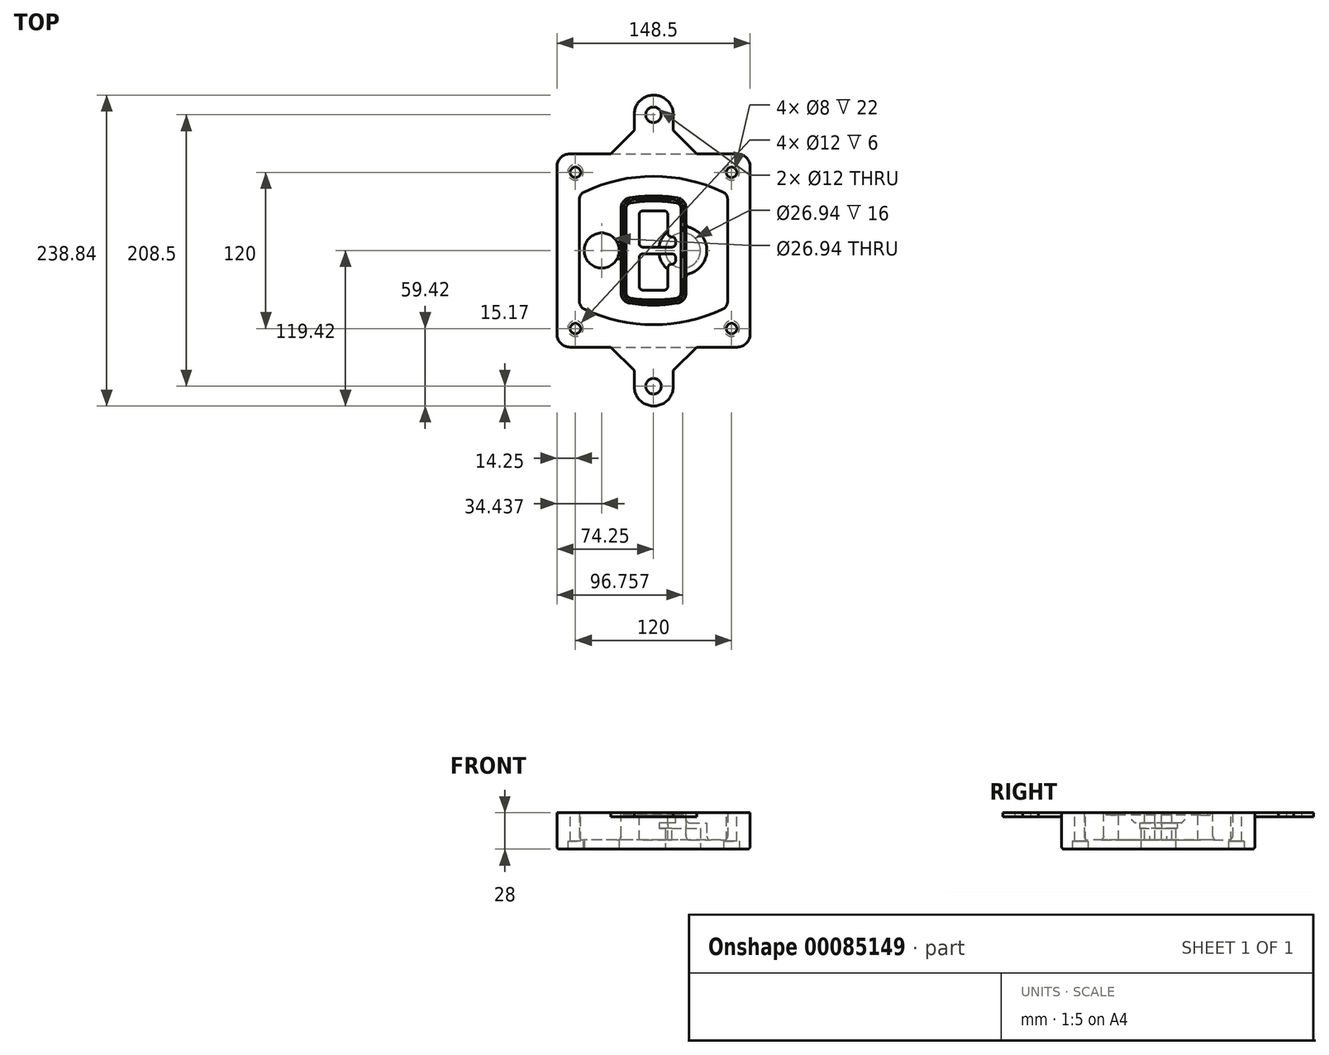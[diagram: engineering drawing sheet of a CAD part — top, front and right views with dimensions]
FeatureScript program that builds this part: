
annotation { "Feature Type Name" : "Feature", "Feature Type Description" : "" }
export const myFeature = defineFeature(function(context is Context, id is Id, definition is map)
    precondition{}
    {
        {
            var Q0;
            Q0=qCreatedBy(makeId("Top.planeOp"),FACE);
            var sketch = newSketch(context, id + "F0", { "sketchPlane" : qUnion([Q0])});
            skPoint(sketch, "E0.rect.middle", {"position": v(0, 0) * mm});
            skLineSegment(sketch, "E1.bottom", {"start": v(-64.25, -74.25) * mm, "end": v(64.25, -74.25) * mm});
            skLineSegment(sketch, "E1.top", {"start": v(-64.25, 74.25) * mm, "end": v(64.25, 74.25) * mm});
            skLineSegment(sketch, "E1.left", {"start": v(-74.25, -64.25) * mm, "end": v(-74.25, 64.25) * mm});
            skLineSegment(sketch, "E1.right", {"start": v(74.25, -64.25) * mm, "end": v(74.25, 64.25) * mm});
            skLineSegment(sketch, "E2", {"start": v(-74.25, 74.25) * mm, "end": v(74.25, -74.25) * mm, "construction": true});
            skLineSegment(sketch, "E3", {"start": v(74.25, 74.25) * mm, "end": v(-74.25, -74.25) * mm, "construction": true});
            skCircle(sketch, "E4", {"center": v(-60, 60) * mm, "radius": 4 * mm});
            skCircle(sketch, "E5", {"center": v(60, 60) * mm, "radius": 4 * mm});
            skCircle(sketch, "E6", {"center": v(60, -60) * mm, "radius": 4 * mm});
            skCircle(sketch, "E7", {"center": v(-60, -60) * mm, "radius": 4 * mm});
            skLineSegment(sketch, "E8", {"start": v(-60, 60) * mm, "end": v(60, 60) * mm, "construction": true});
            skLineSegment(sketch, "E9", {"start": v(60, 60) * mm, "end": v(60, -60) * mm, "construction": true});
            skLineSegment(sketch, "E10", {"start": v(60, -60) * mm, "end": v(-60, -60) * mm, "construction": true});
            skLineSegment(sketch, "E11", {"start": v(-60, -60) * mm, "end": v(-60, 60) * mm, "construction": true});
            skLineSegment(sketch, "E12", {"start": v(-60, 38.83) * mm, "end": v(-60, -38.83) * mm});
            skLineSegment(sketch, "E13", {"start": v(60, 38.83) * mm, "end": v(60, -38.83) * mm});
            skArc(sketch, "E14", {"start": v(54.26, 47.88) * mm, "mid": v(0, 60) * mm, "end": v(-54.26, 47.88) * mm});
            skArc(sketch, "E15", {"start": v(-54.26, -47.88) * mm, "mid": v(0, -60) * mm, "end": v(54.26, -47.88) * mm});
            skLineSegment(sketch, "E16", {"start": v(-60, 0) * mm, "end": v(60, 0) * mm, "construction": true});
            skPoint(sketch, "E17.visualSharp", {"position": v(-60, -45) * mm});
            skArc(sketch, "E17.filletArc", {"start": v(-60, -38.83) * mm, "mid": v(-58.44, -44.2) * mm, "end": v(-54.26, -47.88) * mm});
            skPoint(sketch, "E18.visualSharp", {"position": v(-60, 45) * mm});
            skArc(sketch, "E18.filletArc", {"start": v(-54.26, 47.88) * mm, "mid": v(-58.44, 44.2) * mm, "end": v(-60, 38.83) * mm});
            skPoint(sketch, "E19.visualSharp", {"position": v(60, 45) * mm});
            skArc(sketch, "E19.filletArc", {"start": v(60, 38.83) * mm, "mid": v(58.44, 44.2) * mm, "end": v(54.26, 47.88) * mm});
            skPoint(sketch, "E20.visualSharp", {"position": v(60, -45) * mm});
            skArc(sketch, "E20.filletArc", {"start": v(54.26, -47.88) * mm, "mid": v(58.44, -44.2) * mm, "end": v(60, -38.83) * mm});
            skPoint(sketch, "E21.visualSharp", {"position": v(-74.25, 74.25) * mm});
            skArc(sketch, "E21.filletArc", {"start": v(-64.25, 74.25) * mm, "mid": v(-71.32, 71.32) * mm, "end": v(-74.25, 64.25) * mm});
            skPoint(sketch, "E22.visualSharp", {"position": v(74.25, 74.25) * mm});
            skArc(sketch, "E22.filletArc", {"start": v(74.25, 64.25) * mm, "mid": v(71.32, 71.32) * mm, "end": v(64.25, 74.25) * mm});
            skPoint(sketch, "E23.visualSharp", {"position": v(74.25, -74.25) * mm});
            skArc(sketch, "E23.filletArc", {"start": v(64.25, -74.25) * mm, "mid": v(71.32, -71.32) * mm, "end": v(74.25, -64.25) * mm});
            skPoint(sketch, "E24.visualSharp", {"position": v(-74.25, -74.25) * mm});
            skArc(sketch, "E24.filletArc", {"start": v(-74.25, -64.25) * mm, "mid": v(-71.32, -71.32) * mm, "end": v(-64.25, -74.25) * mm});
            skArc(sketch, "E25.0", {"start": v(57, 38.83) * mm, "mid": v(55.9, 42.58) * mm, "end": v(52.98, 45.17) * mm});
            skLineSegment(sketch, "E25.1", {"start": v(57, 38.83) * mm, "end": v(57, -38.83) * mm});
            skArc(sketch, "E25.2", {"start": v(52.98, -45.17) * mm, "mid": v(55.9, -42.58) * mm, "end": v(57, -38.83) * mm});
            skArc(sketch, "E25.3", {"start": v(-52.98, -45.17) * mm, "mid": v(0, -57) * mm, "end": v(52.98, -45.17) * mm});
            skArc(sketch, "E25.4", {"start": v(-57, -38.83) * mm, "mid": v(-55.9, -42.58) * mm, "end": v(-52.98, -45.17) * mm});
            skArc(sketch, "E25.5", {"start": v(52.98, 45.17) * mm, "mid": v(0, 57) * mm, "end": v(-52.98, 45.17) * mm});
            skLineSegment(sketch, "E25.6", {"start": v(-57, 38.83) * mm, "end": v(-57, -38.83) * mm});
            skArc(sketch, "E25.7", {"start": v(-52.98, 45.17) * mm, "mid": v(-55.9, 42.58) * mm, "end": v(-57, 38.83) * mm});
            skArc(sketch, "E26.0", {"start": v(-55.96, 51.5) * mm, "mid": v(-61.82, 46.33) * mm, "end": v(-64, 38.83) * mm});
            skArc(sketch, "E26.1", {"start": v(55.96, 51.5) * mm, "mid": v(0, 64) * mm, "end": v(-55.96, 51.5) * mm});
            skArc(sketch, "E26.2", {"start": v(64, 38.83) * mm, "mid": v(61.82, 46.33) * mm, "end": v(55.96, 51.5) * mm});
            skLineSegment(sketch, "E26.3", {"start": v(64, 38.83) * mm, "end": v(64, -38.83) * mm});
            skArc(sketch, "E26.4", {"start": v(55.96, -51.5) * mm, "mid": v(61.82, -46.33) * mm, "end": v(64, -38.83) * mm});
            skLineSegment(sketch, "E26.5", {"start": v(-64, 38.83) * mm, "end": v(-64, -38.83) * mm});
            skArc(sketch, "E26.6", {"start": v(-55.96, -51.5) * mm, "mid": v(0, -64) * mm, "end": v(55.96, -51.5) * mm});
            skArc(sketch, "E26.7", {"start": v(-64, -38.83) * mm, "mid": v(-61.82, -46.33) * mm, "end": v(-55.96, -51.5) * mm});
            skSolve(sketch);
        }
        {
            var Q0;
            Q0=makeQuery(id+"F0.imprint","IMPRINT",FACE,{"disambiguationData":[TD([[makeQuery(id+"F0.imprint","IMPRINT",EDGE,{"derivedFrom":sQuery(id+"F0.wireOp",EDGE,"E1.bottom")}),1.0]])]});
            var Q1;
            Q1=makeQuery(id+"F0.imprint","IMPRINT",FACE,{"disambiguationData":[TD([[makeQuery(id+"F0.imprint","IMPRINT",EDGE,{"derivedFrom":sQuery(id+"F0.wireOp",EDGE,"E12")}),1.0]])]});
            var Q2;
            Q2=makeQuery(id+"F0.imprint","IMPRINT",FACE,{"disambiguationData":[TD([[makeQuery(id+"F0.imprint","IMPRINT",EDGE,{"derivedFrom":sQuery(id+"F0.wireOp",EDGE,"E25.0")}),1.0]])]});
            var Q3;
            Q3=makeQuery(id+"F0.imprint","IMPRINT",FACE,{"disambiguationData":[TD([[makeQuery(id+"F0.imprint","IMPRINT",EDGE,{"derivedFrom":sQuery(id+"F0.wireOp",EDGE,"E12")}),-1.0]])]});
            extrude(context, id + "F1", {"entities" : qUnion([Q0, Q1, Q2, Q3]), "oppositeDirection" : true, "depth" : 25 * mm});
        }
        {
            var Q0;
            Q0=makeQuery(id+"F0.imprint","IMPRINT",FACE,{"disambiguationData":[TD([[makeQuery(id+"F0.imprint","IMPRINT",EDGE,{"derivedFrom":sQuery(id+"F0.wireOp",EDGE,"E12")}),1.0]])]});
            extrude(context, id + "F2", {"entities" : qUnion([Q0]), "operationType" : NewBodyOperationType.ADD, "depth" : 3 * mm});
        }
        {
            var Q0;
            Q0=makeQuery(id+"F0.imprint","IMPRINT",FACE,{"disambiguationData":[TD([[makeQuery(id+"F0.imprint","IMPRINT",EDGE,{"derivedFrom":sQuery(id+"F0.wireOp",EDGE,"E25.0")}),1.0]])]});
            extrude(context, id + "F3", {"entities" : qUnion([Q0]), "operationType" : NewBodyOperationType.REMOVE, "oppositeDirection" : true, "depth" : 18 * mm});
        }
        {
            var Q0;
            Q0=makeQuery(id+"F2.opExtrude","CAP_FACE",FACE,{"disambiguationData":[OSD([sQuery(id+"F0.wireOp",EDGE,"E12"),sQuery(id+"F0.wireOp",EDGE,"E13"),sQuery(id+"F0.wireOp",EDGE,"E14"),sQuery(id+"F0.wireOp",EDGE,"E15"),sQuery(id+"F0.wireOp",EDGE,"E17.filletArc"),sQuery(id+"F0.wireOp",EDGE,"E18.filletArc"),sQuery(id+"F0.wireOp",EDGE,"E19.filletArc"),sQuery(id+"F0.wireOp",EDGE,"E20.filletArc"),sQuery(id+"F0.wireOp",EDGE,"E25.0"),sQuery(id+"F0.wireOp",EDGE,"E25.1"),sQuery(id+"F0.wireOp",EDGE,"E25.2"),sQuery(id+"F0.wireOp",EDGE,"E25.3"),sQuery(id+"F0.wireOp",EDGE,"E25.4"),sQuery(id+"F0.wireOp",EDGE,"E25.5"),sQuery(id+"F0.wireOp",EDGE,"E25.6"),sQuery(id+"F0.wireOp",EDGE,"E25.7")])],"isStart":false});
            var sketch = newSketch(context, id + "F4", { "sketchPlane" : qUnion([Q0])});
            skArc(sketch, "E27.0", {"start": v(-18.34, -40.45) * mm, "mid": v(0, -42) * mm, "end": v(18.34, -40.45) * mm});
            skArc(sketch, "E28.0", {"start": v(18.34, 40.45) * mm, "mid": v(0, 42) * mm, "end": v(-18.34, 40.45) * mm});
            skLineSegment(sketch, "E29", {"start": v(-25, 32.57) * mm, "end": v(-25, -32.57) * mm});
            skLineSegment(sketch, "E30", {"start": v(25, 32.57) * mm, "end": v(25, -32.57) * mm});
            skLineSegment(sketch, "E31", {"start": v(-25, 39.1) * mm, "end": v(25, 39.1) * mm, "construction": true});
            skLineSegment(sketch, "E32", {"start": v(-25, -39.1) * mm, "end": v(25, -39.1) * mm, "construction": true});
            skPoint(sketch, "E33.visualSharp", {"position": v(-25, 39.1) * mm});
            skArc(sketch, "E33.filletArc", {"start": v(-18.34, 40.45) * mm, "mid": v(-23.11, 37.73) * mm, "end": v(-25, 32.57) * mm});
            skPoint(sketch, "E34.visualSharp", {"position": v(25, 39.1) * mm});
            skArc(sketch, "E34.filletArc", {"start": v(25, 32.57) * mm, "mid": v(23.11, 37.73) * mm, "end": v(18.34, 40.45) * mm});
            skPoint(sketch, "E35.visualSharp", {"position": v(25, -39.1) * mm});
            skArc(sketch, "E35.filletArc", {"start": v(18.34, -40.45) * mm, "mid": v(23.11, -37.73) * mm, "end": v(25, -32.57) * mm});
            skPoint(sketch, "E36.visualSharp", {"position": v(-25, -39.1) * mm});
            skArc(sketch, "E36.filletArc", {"start": v(-25, -32.57) * mm, "mid": v(-23.11, -37.73) * mm, "end": v(-18.34, -40.45) * mm});
            skArc(sketch, "E37.0", {"start": v(52.98, 45.17) * mm, "mid": v(0, 57) * mm, "end": v(-52.98, 45.17) * mm});
            skArc(sketch, "E37.1", {"start": v(-52.98, 45.17) * mm, "mid": v(-55.9, 42.58) * mm, "end": v(-57, 38.83) * mm});
            skLineSegment(sketch, "E37.2", {"start": v(-57, 38.83) * mm, "end": v(-57, -38.83) * mm});
            skArc(sketch, "E37.3", {"start": v(-57, -38.83) * mm, "mid": v(-55.9, -42.58) * mm, "end": v(-52.98, -45.17) * mm});
            skArc(sketch, "E37.4", {"start": v(-52.98, -45.17) * mm, "mid": v(0, -57) * mm, "end": v(52.98, -45.17) * mm});
            skArc(sketch, "E37.5", {"start": v(52.98, -45.17) * mm, "mid": v(55.9, -42.58) * mm, "end": v(57, -38.83) * mm});
            skLineSegment(sketch, "E37.6", {"start": v(57, 38.83) * mm, "end": v(57, -38.83) * mm});
            skArc(sketch, "E37.7", {"start": v(57, 38.83) * mm, "mid": v(55.9, 42.58) * mm, "end": v(52.98, 45.17) * mm});
            skLineSegment(sketch, "E38.0", {"start": v(23, 32.57) * mm, "end": v(23, -32.57) * mm});
            skArc(sketch, "E38.1", {"start": v(18, -38.48) * mm, "mid": v(21.58, -36.44) * mm, "end": v(23, -32.57) * mm});
            skArc(sketch, "E38.2", {"start": v(-18, -38.48) * mm, "mid": v(0, -40) * mm, "end": v(18, -38.48) * mm});
            skArc(sketch, "E38.3", {"start": v(-23, -32.57) * mm, "mid": v(-21.58, -36.44) * mm, "end": v(-18, -38.48) * mm});
            skLineSegment(sketch, "E38.4", {"start": v(-23, 32.57) * mm, "end": v(-23, -32.57) * mm});
            skArc(sketch, "E38.5", {"start": v(23, 32.57) * mm, "mid": v(21.58, 36.44) * mm, "end": v(18, 38.48) * mm});
            skArc(sketch, "E38.6", {"start": v(-18, 38.48) * mm, "mid": v(-21.58, 36.44) * mm, "end": v(-23, 32.57) * mm});
            skArc(sketch, "E38.7", {"start": v(18, 38.48) * mm, "mid": v(0, 40) * mm, "end": v(-18, 38.48) * mm});
            skArc(sketch, "E39.0", {"start": v(21, 32.57) * mm, "mid": v(20.06, 35.15) * mm, "end": v(17.67, 36.5) * mm});
            skLineSegment(sketch, "E39.1", {"start": v(21, 32.57) * mm, "end": v(21, -32.57) * mm});
            skArc(sketch, "E39.2", {"start": v(17.67, -36.5) * mm, "mid": v(20.06, -35.15) * mm, "end": v(21, -32.57) * mm});
            skArc(sketch, "E39.3", {"start": v(-17.67, -36.5) * mm, "mid": v(0, -38) * mm, "end": v(17.67, -36.5) * mm});
            skArc(sketch, "E39.4", {"start": v(-21, -32.57) * mm, "mid": v(-20.06, -35.15) * mm, "end": v(-17.67, -36.5) * mm});
            skArc(sketch, "E39.5", {"start": v(17.67, 36.5) * mm, "mid": v(0, 38) * mm, "end": v(-17.67, 36.5) * mm});
            skLineSegment(sketch, "E39.6", {"start": v(-21, 32.57) * mm, "end": v(-21, -32.57) * mm});
            skArc(sketch, "E39.7", {"start": v(-17.67, 36.5) * mm, "mid": v(-20.06, 35.15) * mm, "end": v(-21, 32.57) * mm});
            skLineSegment(sketch, "E40", {"start": v(-25, 0) * mm, "end": v(25, 0) * mm, "construction": true});
            skLineSegment(sketch, "E41", {"start": v(-11, 5.5) * mm, "end": v(-11, 27.5) * mm});
            skLineSegment(sketch, "E42", {"start": v(-8, 30.5) * mm, "end": v(8, 30.5) * mm});
            skLineSegment(sketch, "E43", {"start": v(11, 27.5) * mm, "end": v(11, 13.5) * mm});
            skLineSegment(sketch, "E44", {"start": v(14, 10.5) * mm, "end": v(14, 10.5) * mm});
            skLineSegment(sketch, "E45", {"start": v(17, 7.5) * mm, "end": v(17, 5.5) * mm});
            skLineSegment(sketch, "E46", {"start": v(14, 2.5) * mm, "end": v(-8, 2.5) * mm});
            skPoint(sketch, "E47.visualSharp", {"position": v(-11, 30.5) * mm});
            skArc(sketch, "E47.filletArc", {"start": v(-8, 30.5) * mm, "mid": v(-10.12, 29.62) * mm, "end": v(-11, 27.5) * mm});
            skPoint(sketch, "E48.visualSharp", {"position": v(11, 30.5) * mm});
            skArc(sketch, "E48.filletArc", {"start": v(11, 27.5) * mm, "mid": v(10.12, 29.62) * mm, "end": v(8, 30.5) * mm});
            skPoint(sketch, "E49.visualSharp", {"position": v(11, 10.5) * mm});
            skArc(sketch, "E49.filletArc", {"start": v(11, 13.5) * mm, "mid": v(11.88, 11.38) * mm, "end": v(14, 10.5) * mm});
            skPoint(sketch, "E50.visualSharp", {"position": v(17, 10.5) * mm});
            skArc(sketch, "E50.filletArc", {"start": v(17, 7.5) * mm, "mid": v(16.12, 9.62) * mm, "end": v(14, 10.5) * mm});
            skPoint(sketch, "E51.visualSharp", {"position": v(17, 2.5) * mm});
            skArc(sketch, "E51.filletArc", {"start": v(14, 2.5) * mm, "mid": v(16.12, 3.38) * mm, "end": v(17, 5.5) * mm});
            skPoint(sketch, "E52.visualSharp", {"position": v(-11, 2.5) * mm});
            skArc(sketch, "E52.filletArc", {"start": v(-11, 5.5) * mm, "mid": v(-10.12, 3.38) * mm, "end": v(-8, 2.5) * mm});
            skLineSegment(sketch, "E53.0.MirrorCS", {"start": v(14, -2.5) * mm, "end": v(-8, -2.5) * mm});
            skArc(sketch, "E54.0.MirrorCS", {"start": v(-11, -5.5) * mm, "mid": v(-10.12, -3.38) * mm, "end": v(-8, -2.5) * mm});
            skLineSegment(sketch, "E55.0.MirrorCS", {"start": v(-11, -5.5) * mm, "end": v(-11, -27.5) * mm});
            skArc(sketch, "E56.0.MirrorCS", {"start": v(-8, -30.5) * mm, "mid": v(-10.12, -29.62) * mm, "end": v(-11, -27.5) * mm});
            skLineSegment(sketch, "E57.0.MirrorCS", {"start": v(-8, -30.5) * mm, "end": v(8, -30.5) * mm});
            skArc(sketch, "E58.0.MirrorCS", {"start": v(11, -27.5) * mm, "mid": v(10.12, -29.62) * mm, "end": v(8, -30.5) * mm});
            skLineSegment(sketch, "E59.0.MirrorCS", {"start": v(11, -27.5) * mm, "end": v(11, -13.5) * mm});
            skArc(sketch, "E60.0.MirrorCS", {"start": v(11, -13.5) * mm, "mid": v(11.88, -11.38) * mm, "end": v(14, -10.5) * mm});
            skArc(sketch, "E61.0.MirrorCS", {"start": v(17, -7.5) * mm, "mid": v(16.12, -9.62) * mm, "end": v(14, -10.5) * mm});
            skLineSegment(sketch, "E62.0.MirrorCS", {"start": v(17, -7.5) * mm, "end": v(17, -5.5) * mm});
            skArc(sketch, "E63.0.MirrorCS", {"start": v(14, -2.5) * mm, "mid": v(16.12, -3.38) * mm, "end": v(17, -5.5) * mm});
            skSolve(sketch);
        }
        {
            var Q0;
            Q0=makeQuery(id+"F4.imprint","IMPRINT",FACE,{"disambiguationData":[TD([[makeQuery(id+"F4.imprint","IMPRINT",EDGE,{"derivedFrom":sQuery(id+"F4.wireOp",EDGE,"E27.0")}),1.0]])]});
            var Q1;
            Q1=makeQuery(id+"F4.imprint","IMPRINT",FACE,{"disambiguationData":[TD([[makeQuery(id+"F4.imprint","IMPRINT",EDGE,{"derivedFrom":sQuery(id+"F4.wireOp",EDGE,"E38.0")}),-1.0]])]});
            var Q2;
            Q2=makeQuery(id+"F4.imprint","IMPRINT",FACE,{"disambiguationData":[TD([[makeQuery(id+"F4.imprint","IMPRINT",EDGE,{"derivedFrom":sQuery(id+"F4.wireOp",EDGE,"E39.0")}),1.0]])]});
            extrude(context, id + "F5", {"entities" : qUnion([Q0, Q1, Q2]), "operationType" : NewBodyOperationType.ADD, "endBound" : BoundingType.UP_TO_NEXT, "oppositeDirection" : true, "depth" : 25 * mm});
        }
        {
            var Q0;
            Q0=makeQuery(id+"F4.imprint","IMPRINT",FACE,{"disambiguationData":[TD([[makeQuery(id+"F4.imprint","IMPRINT",EDGE,{"derivedFrom":sQuery(id+"F4.wireOp",EDGE,"E38.0")}),-1.0]])]});
            extrude(context, id + "F6", {"entities" : qUnion([Q0]), "operationType" : NewBodyOperationType.REMOVE, "oppositeDirection" : true, "depth" : 2 * mm});
        }
        {
            var Q0;
            Q0=makeQuery(id+"F1.opExtrude","CAP_FACE",FACE,{"disambiguationData":[OSD([sQuery(id+"F0.wireOp",EDGE,"E1.bottom"),sQuery(id+"F0.wireOp",EDGE,"E1.top"),sQuery(id+"F0.wireOp",EDGE,"E1.left"),sQuery(id+"F0.wireOp",EDGE,"E1.right"),sQuery(id+"F0.wireOp",EDGE,"E4"),sQuery(id+"F0.wireOp",EDGE,"E5"),sQuery(id+"F0.wireOp",EDGE,"E6"),sQuery(id+"F0.wireOp",EDGE,"E7"),sQuery(id+"F0.wireOp",EDGE,"E21.filletArc"),sQuery(id+"F0.wireOp",EDGE,"E22.filletArc"),sQuery(id+"F0.wireOp",EDGE,"E23.filletArc"),sQuery(id+"F0.wireOp",EDGE,"E24.filletArc")])],"isStart":false});
            var sketch = newSketch(context, id + "F7", { "sketchPlane" : qUnion([Q0])});
            skCircle(sketch, "E64", {"center": v(22.5, 0) * mm, "radius": 13.47 * mm});
            skCircle(sketch, "E65", {"center": v(-39.81, 0) * mm, "radius": 13.47 * mm});
            skLineSegment(sketch, "E66", {"start": v(74.25, 0) * mm, "end": v(-74.25, 0) * mm});
            skCircle(sketch, "E67", {"center": v(22.5, 0) * mm, "radius": 18.47 * mm});
            skCircle(sketch, "E68", {"center": v(60, -60) * mm, "radius": 6 * mm});
            skCircle(sketch, "E69", {"center": v(-60, -60) * mm, "radius": 6 * mm});
            skCircle(sketch, "E70", {"center": v(-60, 60) * mm, "radius": 6 * mm});
            skCircle(sketch, "E71", {"center": v(60, 60) * mm, "radius": 6 * mm});
            skSolve(sketch);
        }
        {
            var Q0;
            {var subQ1=sQuery(id+"F7.wireOp",EDGE,"E66");var subQ4=sQuery(id+"F7.wireOp",EDGE,"E64");var subQ6=makeQuery(id+"F7.imprint","INTERSECT",VERTEX,{"disambiguationData":[OD(0.0)],"derivedFrom":[subQ4,subQ1]});Q0=makeQuery(id+"F7.imprint","IMPRINT",FACE,{"disambiguationData":[TD([[makeQuery(id+"F7.imprint","IMPRINT",EDGE,{"disambiguationData":[TD([[subQ6,-1.0]])],"derivedFrom":subQ4}),-1.0]])]});}
            var Q1;
            {var subQ0=sQuery(id+"F7.wireOp",EDGE,"E66");var subQ1=sQuery(id+"F7.wireOp",EDGE,"E64");var subQ3=makeQuery(id+"F7.imprint","INTERSECT",VERTEX,{"disambiguationData":[OD(0.0)],"derivedFrom":[subQ1,subQ0]});Q1=makeQuery(id+"F7.imprint","IMPRINT",FACE,{"disambiguationData":[TD([[makeQuery(id+"F7.imprint","IMPRINT",EDGE,{"disambiguationData":[TD([[subQ3,-1.0]])],"derivedFrom":subQ1}),1.0]])]});}
            var Q2;
            {var subQ0=sQuery(id+"F7.wireOp",EDGE,"E66");var subQ1=sQuery(id+"F7.wireOp",EDGE,"E64");var subQ3=makeQuery(id+"F7.imprint","INTERSECT",VERTEX,{"disambiguationData":[OD(0.0)],"derivedFrom":[subQ1,subQ0]});Q2=makeQuery(id+"F7.imprint","IMPRINT",FACE,{"disambiguationData":[TD([[makeQuery(id+"F7.imprint","IMPRINT",EDGE,{"disambiguationData":[TD([[subQ3,1.0]])],"derivedFrom":subQ1}),1.0]])]});}
            var Q3;
            {var subQ1=sQuery(id+"F7.wireOp",EDGE,"E66");var subQ4=sQuery(id+"F7.wireOp",EDGE,"E64");var subQ6=makeQuery(id+"F7.imprint","INTERSECT",VERTEX,{"disambiguationData":[OD(0.0)],"derivedFrom":[subQ4,subQ1]});Q3=makeQuery(id+"F7.imprint","IMPRINT",FACE,{"disambiguationData":[TD([[makeQuery(id+"F7.imprint","IMPRINT",EDGE,{"disambiguationData":[TD([[subQ6,1.0]])],"derivedFrom":subQ4}),-1.0]])]});}
            extrude(context, id + "F8", {"entities" : qUnion([Q0, Q1, Q2, Q3]), "operationType" : NewBodyOperationType.ADD, "oppositeDirection" : true, "depth" : 20 * mm});
        }
        {
            var Q0;
            {var subQ0=sQuery(id+"F7.wireOp",EDGE,"E66");var subQ1=sQuery(id+"F7.wireOp",EDGE,"E64");var subQ3=makeQuery(id+"F7.imprint","INTERSECT",VERTEX,{"disambiguationData":[OD(0.0)],"derivedFrom":[subQ1,subQ0]});Q0=makeQuery(id+"F7.imprint","IMPRINT",FACE,{"disambiguationData":[TD([[makeQuery(id+"F7.imprint","IMPRINT",EDGE,{"disambiguationData":[TD([[subQ3,-1.0]])],"derivedFrom":subQ1}),1.0]])]});}
            var Q1;
            {var subQ0=sQuery(id+"F7.wireOp",EDGE,"E66");var subQ1=sQuery(id+"F7.wireOp",EDGE,"E64");var subQ3=makeQuery(id+"F7.imprint","INTERSECT",VERTEX,{"disambiguationData":[OD(0.0)],"derivedFrom":[subQ1,subQ0]});Q1=makeQuery(id+"F7.imprint","IMPRINT",FACE,{"disambiguationData":[TD([[makeQuery(id+"F7.imprint","IMPRINT",EDGE,{"disambiguationData":[TD([[subQ3,1.0]])],"derivedFrom":subQ1}),1.0]])]});}
            extrude(context, id + "F9", {"entities" : qUnion([Q0, Q1]), "operationType" : NewBodyOperationType.REMOVE, "oppositeDirection" : true, "depth" : 16 * mm});
        }
        {
            var Q0;
            {var subQ0=sQuery(id+"F7.wireOp",EDGE,"E66");var subQ1=sQuery(id+"F7.wireOp",EDGE,"E65");var subQ3=makeQuery(id+"F7.imprint","INTERSECT",VERTEX,{"disambiguationData":[OD(0.0)],"derivedFrom":[subQ1,subQ0]});Q0=makeQuery(id+"F7.imprint","IMPRINT",FACE,{"disambiguationData":[TD([[makeQuery(id+"F7.imprint","IMPRINT",EDGE,{"disambiguationData":[TD([[subQ3,-1.0]])],"derivedFrom":subQ1}),1.0]])]});}
            var Q1;
            {var subQ0=sQuery(id+"F7.wireOp",EDGE,"E66");var subQ1=sQuery(id+"F7.wireOp",EDGE,"E65");var subQ3=makeQuery(id+"F7.imprint","INTERSECT",VERTEX,{"disambiguationData":[OD(0.0)],"derivedFrom":[subQ1,subQ0]});Q1=makeQuery(id+"F7.imprint","IMPRINT",FACE,{"disambiguationData":[TD([[makeQuery(id+"F7.imprint","IMPRINT",EDGE,{"disambiguationData":[TD([[subQ3,1.0]])],"derivedFrom":subQ1}),1.0]])]});}
            extrude(context, id + "F10", {"entities" : qUnion([Q0, Q1]), "operationType" : NewBodyOperationType.REMOVE, "oppositeDirection" : true, "depth" : 25 * mm});
        }
        {
            var Q0;
            Q0=makeQuery(id+"F7.imprint","IMPRINT",FACE,{"disambiguationData":[TD([[makeQuery(id+"F7.imprint","IMPRINT",EDGE,{"derivedFrom":sQuery(id+"F7.wireOp",EDGE,"E68")}),1.0]])]});
            var Q1;
            Q1=makeQuery(id+"F7.imprint","IMPRINT",FACE,{"disambiguationData":[TD([[makeQuery(id+"F7.imprint","IMPRINT",EDGE,{"derivedFrom":makeQuery(id+"F1.opExtrude","CAP_EDGE",EDGE,{"disambiguationData":[OSD([sQuery(id+"F0.wireOp",EDGE,"E5")])],"isStart":false})}),-1.0]])]});
            var Q2;
            Q2=makeQuery(id+"F7.imprint","IMPRINT",FACE,{"disambiguationData":[TD([[makeQuery(id+"F7.imprint","IMPRINT",EDGE,{"derivedFrom":sQuery(id+"F7.wireOp",EDGE,"E69")}),1.0]])]});
            var Q3;
            Q3=makeQuery(id+"F7.imprint","IMPRINT",FACE,{"disambiguationData":[TD([[makeQuery(id+"F7.imprint","IMPRINT",EDGE,{"derivedFrom":makeQuery(id+"F1.opExtrude","CAP_EDGE",EDGE,{"disambiguationData":[OSD([sQuery(id+"F0.wireOp",EDGE,"E4")])],"isStart":false})}),-1.0]])]});
            var Q4;
            Q4=makeQuery(id+"F7.imprint","IMPRINT",FACE,{"disambiguationData":[TD([[makeQuery(id+"F7.imprint","IMPRINT",EDGE,{"derivedFrom":sQuery(id+"F7.wireOp",EDGE,"E70")}),1.0]])]});
            var Q5;
            Q5=makeQuery(id+"F7.imprint","IMPRINT",FACE,{"disambiguationData":[TD([[makeQuery(id+"F7.imprint","IMPRINT",EDGE,{"derivedFrom":makeQuery(id+"F1.opExtrude","CAP_EDGE",EDGE,{"disambiguationData":[OSD([sQuery(id+"F0.wireOp",EDGE,"E7")])],"isStart":false})}),-1.0]])]});
            var Q6;
            Q6=makeQuery(id+"F7.imprint","IMPRINT",FACE,{"disambiguationData":[TD([[makeQuery(id+"F7.imprint","IMPRINT",EDGE,{"derivedFrom":sQuery(id+"F7.wireOp",EDGE,"E71")}),1.0]])]});
            var Q7;
            Q7=makeQuery(id+"F7.imprint","IMPRINT",FACE,{"disambiguationData":[TD([[makeQuery(id+"F7.imprint","IMPRINT",EDGE,{"derivedFrom":makeQuery(id+"F1.opExtrude","CAP_EDGE",EDGE,{"disambiguationData":[OSD([sQuery(id+"F0.wireOp",EDGE,"E6")])],"isStart":false})}),-1.0]])]});
            extrude(context, id + "F11", {"entities" : qUnion([Q0, Q1, Q2, Q3, Q4, Q5, Q6, Q7]), "operationType" : NewBodyOperationType.REMOVE, "oppositeDirection" : true, "depth" : 6 * mm});
        }
        {
            var Q0;
            Q0=makeQuery(id+"F9.boolean.opBoolean","COPY",FACE,{"derivedFrom":makeQuery(id+"F9.opExtrude","CAP_FACE",FACE,{"disambiguationData":[OSD([sQuery(id+"F7.wireOp",EDGE,"E64")])],"isStart":false})});
            var sketch = newSketch(context, id + "F12", { "sketchPlane" : qUnion([Q0])});
            skArc(sketch, "E72.0", {"start": v(11, 14.45) * mm, "mid": v(6.45, 9.13) * mm, "end": v(4.2, 2.5) * mm});
            skArc(sketch, "E72.1", {"start": v(4.2, -2.5) * mm, "mid": v(6.45, -9.13) * mm, "end": v(11, -14.45) * mm});
            skLineSegment(sketch, "E73", {"start": v(4.2, -2.5) * mm, "end": v(14, -2.5) * mm});
            skLineSegment(sketch, "E74.0", {"start": v(14, 2.5) * mm, "end": v(4.2, 2.5) * mm});
            skArc(sketch, "E74.1", {"start": v(14, 2.5) * mm, "mid": v(16.12, 3.38) * mm, "end": v(17, 5.5) * mm});
            skLineSegment(sketch, "E74.2", {"start": v(17, 7.5) * mm, "end": v(17, 5.5) * mm});
            skArc(sketch, "E74.3", {"start": v(17, 7.5) * mm, "mid": v(16.12, 9.62) * mm, "end": v(14, 10.5) * mm});
            skArc(sketch, "E74.4", {"start": v(11, 13.5) * mm, "mid": v(11.88, 11.38) * mm, "end": v(14, 10.5) * mm});
            skLineSegment(sketch, "E74.5", {"start": v(11, 14.45) * mm, "end": v(11, 13.5) * mm});
            skLineSegment(sketch, "E74.7", {"start": v(14, -2.5) * mm, "end": v(4.2, -2.5) * mm});
            skArc(sketch, "E74.8", {"start": v(14, -2.5) * mm, "mid": v(16.12, -3.38) * mm, "end": v(17, -5.5) * mm});
            skLineSegment(sketch, "E74.9", {"start": v(17, -7.5) * mm, "end": v(17, -5.5) * mm});
            skArc(sketch, "E74.10", {"start": v(17, -7.5) * mm, "mid": v(16.12, -9.62) * mm, "end": v(14, -10.5) * mm});
            skArc(sketch, "E74.11", {"start": v(11, -13.5) * mm, "mid": v(11.88, -11.38) * mm, "end": v(14, -10.5) * mm});
            skLineSegment(sketch, "E74.12", {"start": v(11, -14.45) * mm, "end": v(11, -13.5) * mm});
            skPoint(sketch, "E75.orphan", {"position": v(11, -27.5) * mm});
            skPoint(sketch, "E76.orphan", {"position": v(-8, -2.5) * mm});
            skPoint(sketch, "E77.orphan", {"position": v(-8, 2.5) * mm});
            skPoint(sketch, "E78.orphan", {"position": v(11, 27.5) * mm});
            skSolve(sketch);
        }
        {
            var Q0;
            {var subQ7=sQuery(id+"F12.wireOp",EDGE,"E72.0");var subQ14=sQuery(id+"F12.wireOp",EDGE,"E72.1");var subQ16=sQuery(id+"F12.wireOp",EDGE,"E74.1");var subQ18=sQuery(id+"F12.wireOp",EDGE,"E74.8");Q0=qUnion([makeQuery(id+"F12.imprint","IMPRINT",FACE,{"disambiguationData":[TD([[makeQuery(id+"F12.imprint","IMPRINT",EDGE,{"derivedFrom":subQ7}),1.0]])]}),makeQuery(id+"F12.imprint","IMPRINT",FACE,{"disambiguationData":[TD([[makeQuery(id+"F12.imprint","IMPRINT",EDGE,{"derivedFrom":subQ14}),1.0]])]}),makeQuery(id+"F12.imprint","IMPRINT",FACE,{"disambiguationData":[TD([[makeQuery(id+"F12.imprint","IMPRINT",EDGE,{"derivedFrom":subQ16}),1.0]])]}),makeQuery(id+"F12.imprint","IMPRINT",FACE,{"disambiguationData":[TD([[makeQuery(id+"F12.imprint","IMPRINT",EDGE,{"derivedFrom":subQ18}),-1.0]])]})]);}
            var Q1;
            Q1=makeQuery(id+"F5.boolean.opBoolean","SPLIT",FACE,{"disambiguationData":[TD([makeQuery(id+"F5.opExtrude","SWEPT_FACE",FACE,{"disambiguationData":[OSD([sQuery(id+"F4.wireOp",EDGE,"E41")])]})])],"derivedFrom":makeQuery(id+"F3.boolean.opBoolean","COPY",FACE,{"derivedFrom":makeQuery(id+"F3.opExtrude","CAP_FACE",FACE,{"disambiguationData":[OSD([sQuery(id+"F0.wireOp",EDGE,"E25.0"),sQuery(id+"F0.wireOp",EDGE,"E25.1"),sQuery(id+"F0.wireOp",EDGE,"E25.2"),sQuery(id+"F0.wireOp",EDGE,"E25.3"),sQuery(id+"F0.wireOp",EDGE,"E25.4"),sQuery(id+"F0.wireOp",EDGE,"E25.5"),sQuery(id+"F0.wireOp",EDGE,"E25.6"),sQuery(id+"F0.wireOp",EDGE,"E25.7")])],"isStart":false})})});
            extrude(context, id + "F13", {"entities" : qUnion([Q0]), "operationType" : NewBodyOperationType.REMOVE, "endBound" : BoundingType.UP_TO_SURFACE, "endBoundEntityFace" : qUnion([Q1]), "depth" : 25 * mm});
        }
        {
            var Q0;
            Q0=makeQuery(id+"F3.boolean.opBoolean","COPY",EDGE,{"derivedFrom":makeQuery(id+"F3.opExtrude","CAP_EDGE",EDGE,{"disambiguationData":[OSD([sQuery(id+"F0.wireOp",EDGE,"E25.6")])],"isStart":false})});
            var Q1;
            Q1=makeQuery(id+"F8.boolean.opBoolean","INTERSECT",EDGE,{"derivedFrom":[makeQuery(id+"F5.opExtrude","SWEPT_FACE",FACE,{"disambiguationData":[OSD([sQuery(id+"F4.wireOp",EDGE,"E30")])]}),makeQuery(id+"F8.opExtrude","CAP_FACE",FACE,{"disambiguationData":[OSD([sQuery(id+"F7.wireOp",EDGE,"E67")])],"isStart":false})]});
            var Q2;
            Q2=makeQuery(id+"F8.boolean.opBoolean","INTERSECT",EDGE,{"disambiguationData":[OD(1.0)],"derivedFrom":[makeQuery(id+"F5.opExtrude","SWEPT_FACE",FACE,{"disambiguationData":[OSD([sQuery(id+"F4.wireOp",EDGE,"E30")])]}),makeQuery(id+"F8.opExtrude","SWEPT_FACE",FACE,{"disambiguationData":[OSD([sQuery(id+"F7.wireOp",EDGE,"E67")])]})]});
            var Q3;
            {var subQ0=sQuery(id+"F4.wireOp",EDGE,"E30");Q3=makeQuery(id+"F8.boolean.opBoolean","SPLIT",EDGE,{"disambiguationData":[TD([makeQuery(id+"F5.opExtrude","SWEPT_FACE",FACE,{"disambiguationData":[OSD([sQuery(id+"F4.wireOp",EDGE,"E35.filletArc")])]})])],"derivedFrom":makeQuery(id+"F5.opExtrude","CAP_EDGE",EDGE,{"disambiguationData":[OSD([subQ0])],"isStart":false})});}
            var Q4;
            {var subQ0=sQuery(id+"F0.wireOp",EDGE,"E25.7");var subQ1=sQuery(id+"F0.wireOp",EDGE,"E25.1");var subQ2=sQuery(id+"F0.wireOp",EDGE,"E25.6");var subQ3=sQuery(id+"F0.wireOp",EDGE,"E25.5");var subQ4=sQuery(id+"F0.wireOp",EDGE,"E25.4");var subQ5=sQuery(id+"F0.wireOp",EDGE,"E25.0");var subQ6=sQuery(id+"F0.wireOp",EDGE,"E25.2");var subQ7=sQuery(id+"F0.wireOp",EDGE,"E25.3");Q4=makeQuery(id+"F8.boolean.opBoolean","INTERSECT",EDGE,{"derivedFrom":[makeQuery(id+"F5.boolean.opBoolean","SPLIT",FACE,{"disambiguationData":[TD([makeQuery(id+"F2.opExtrude","SWEPT_FACE",FACE,{"disambiguationData":[OSD([subQ5])]})])],"derivedFrom":makeQuery(id+"F3.boolean.opBoolean","COPY",FACE,{"derivedFrom":makeQuery(id+"F3.opExtrude","CAP_FACE",FACE,{"disambiguationData":[OSD([subQ5,subQ1,subQ6,subQ7,subQ4,subQ3,subQ2,subQ0])],"isStart":false})})}),makeQuery(id+"F8.opExtrude","SWEPT_FACE",FACE,{"disambiguationData":[OSD([sQuery(id+"F7.wireOp",EDGE,"E67")])]})]});}
            var Q5;
            Q5=makeQuery(id+"F8.boolean.opBoolean","INTERSECT",EDGE,{"disambiguationData":[OD(0.0)],"derivedFrom":[makeQuery(id+"F5.opExtrude","SWEPT_FACE",FACE,{"disambiguationData":[OSD([sQuery(id+"F4.wireOp",EDGE,"E30")])]}),makeQuery(id+"F8.opExtrude","SWEPT_FACE",FACE,{"disambiguationData":[OSD([sQuery(id+"F7.wireOp",EDGE,"E67")])]})]});
            fillet(context, id + "F14", {"entities" : qUnion([Q0, Q1, Q2, Q3, Q4, Q5]), "radius" : 3 * mm, "tangentPropagation" : true, "allowEdgeOverflow" : false});
        }
        {
            var Q0;
            Q0=makeQuery(id+"F1.opExtrude","CAP_EDGE",EDGE,{"disambiguationData":[OSD([sQuery(id+"F0.wireOp",EDGE,"E1.bottom")])],"isStart":false});
            fillet(context, id + "F15", {"entities" : qUnion([Q0]), "radius" : 2 * mm, "tangentPropagation" : true, "allowEdgeOverflow" : false});
        }
        {
            var Q0;
            {var subQ0=sQuery(id+"F0.wireOp",EDGE,"E22.filletArc");var subQ1=sQuery(id+"F0.wireOp",EDGE,"E7");var subQ2=sQuery(id+"F0.wireOp",EDGE,"E6");var subQ3=sQuery(id+"F0.wireOp",EDGE,"E5");var subQ4=sQuery(id+"F0.wireOp",EDGE,"E4");var subQ5=sQuery(id+"F0.wireOp",EDGE,"E1.bottom");var subQ6=sQuery(id+"F0.wireOp",EDGE,"E21.filletArc");var subQ7=sQuery(id+"F0.wireOp",EDGE,"E1.top");var subQ8=sQuery(id+"F0.wireOp",EDGE,"E1.left");var subQ9=sQuery(id+"F0.wireOp",EDGE,"E1.right");var subQ10=sQuery(id+"F0.wireOp",EDGE,"E23.filletArc");var subQ11=sQuery(id+"F0.wireOp",EDGE,"E24.filletArc");Q0=makeQuery(id+"F2.boolean.opBoolean","SPLIT",FACE,{"disambiguationData":[TD([makeQuery(id+"F1.opExtrude","SWEPT_FACE",FACE,{"disambiguationData":[OSD([subQ5])]})])],"derivedFrom":makeQuery(id+"F1.opExtrude","CAP_FACE",FACE,{"disambiguationData":[OSD([subQ5,subQ7,subQ8,subQ9,subQ4,subQ3,subQ2,subQ1,subQ6,subQ0,subQ10,subQ11])],"isStart":true})});}
            var sketch = newSketch(context, id + "F16", { "sketchPlane" : qUnion([Q0])});
            skLineSegment(sketch, "E79", {"start": v(0, 74.25) * mm, "end": v(0, 104.25) * mm, "construction": true});
            skCircle(sketch, "E80", {"center": v(0, 104.25) * mm, "radius": 6 * mm});
            skArc(sketch, "E81", {"start": v(15.18, 104.25) * mm, "mid": v(0.18, 119.42) * mm, "end": v(-14.82, 104.25) * mm});
            skLineSegment(sketch, "E82", {"start": v(213.76, 0) * mm, "end": v(-150.5, 0) * mm, "construction": true});
            skPoint(sketch, "E82.startSnap0", {"position": v(74.25, 0) * mm});
            skLineSegment(sketch, "E83.MirrorCS", {"start": v(0, -74.25) * mm, "end": v(0, -104.25) * mm, "construction": true});
            skCircle(sketch, "E84.MirrorC", {"center": v(0, -104.25) * mm, "radius": 6 * mm});
            skLineSegment(sketch, "E85", {"start": v(-14.82, 104.25) * mm, "end": v(-14.68, 92.25) * mm});
            skLineSegment(sketch, "E86", {"start": v(15.18, 104.25) * mm, "end": v(15.18, 92.25) * mm});
            skLineSegment(sketch, "E87", {"start": v(15.18, 92.25) * mm, "end": v(33.18, 74.25) * mm});
            skLineSegment(sketch, "E88", {"start": v(-14.68, 92.25) * mm, "end": v(-32.68, 74.25) * mm});
            skLineSegment(sketch, "E89.MirrorCS", {"start": v(-14.68, -92.25) * mm, "end": v(-32.68, -74.25) * mm});
            skLineSegment(sketch, "E90.MirrorCS", {"start": v(-14.82, -104.25) * mm, "end": v(-14.68, -92.25) * mm});
            skArc(sketch, "E91.MirrorCS", {"start": v(15.18, -104.25) * mm, "mid": v(0.18, -119.42) * mm, "end": v(-14.82, -104.25) * mm});
            skLineSegment(sketch, "E92.MirrorCS", {"start": v(15.18, -92.25) * mm, "end": v(33.18, -74.25) * mm});
            skLineSegment(sketch, "E93.MirrorCS", {"start": v(15.18, -104.25) * mm, "end": v(15.18, -92.25) * mm});
            skSolve(sketch);
        }
        {
            var Q0;
            Q0=makeQuery(id+"F16.imprint","IMPRINT",FACE,{"disambiguationData":[TD([[makeQuery(id+"F16.imprint","IMPRINT",EDGE,{"derivedFrom":sQuery(id+"F16.wireOp",EDGE,"E84.MirrorC")}),-1.0]])]});
            var Q1;
            Q1=makeQuery(id+"F16.imprint","IMPRINT",FACE,{"disambiguationData":[TD([[makeQuery(id+"F16.imprint","IMPRINT",EDGE,{"derivedFrom":sQuery(id+"F16.wireOp",EDGE,"E81")}),1.0]])]});
            var Q2;
            Q2=makeQuery(id+"F16.imprint","IMPRINT",FACE,{"disambiguationData":[TD([[makeQuery(id+"F16.imprint","IMPRINT",EDGE,{"derivedFrom":makeQuery(id+"F1.opExtrude","CAP_EDGE",EDGE,{"disambiguationData":[OSD([sQuery(id+"F0.wireOp",EDGE,"E1.left")])],"isStart":true})}),-1.0]])]});
            var Q3;
            Q3=makeQuery(id+"F2.opExtrude","CAP_FACE",FACE,{"disambiguationData":[OSD([sQuery(id+"F0.wireOp",EDGE,"E12"),sQuery(id+"F0.wireOp",EDGE,"E13"),sQuery(id+"F0.wireOp",EDGE,"E14"),sQuery(id+"F0.wireOp",EDGE,"E15"),sQuery(id+"F0.wireOp",EDGE,"E17.filletArc"),sQuery(id+"F0.wireOp",EDGE,"E18.filletArc"),sQuery(id+"F0.wireOp",EDGE,"E19.filletArc"),sQuery(id+"F0.wireOp",EDGE,"E20.filletArc"),sQuery(id+"F0.wireOp",EDGE,"E25.0"),sQuery(id+"F0.wireOp",EDGE,"E25.1"),sQuery(id+"F0.wireOp",EDGE,"E25.2"),sQuery(id+"F0.wireOp",EDGE,"E25.3"),sQuery(id+"F0.wireOp",EDGE,"E25.4"),sQuery(id+"F0.wireOp",EDGE,"E25.5"),sQuery(id+"F0.wireOp",EDGE,"E25.6"),sQuery(id+"F0.wireOp",EDGE,"E25.7")])],"isStart":false});
            extrude(context, id + "F17", {"entities" : qUnion([Q0, Q1, Q2]), "operationType" : NewBodyOperationType.ADD, "endBound" : BoundingType.UP_TO_SURFACE, "endBoundEntityFace" : qUnion([Q3]), "depth" : 25 * mm});
        }
    });
